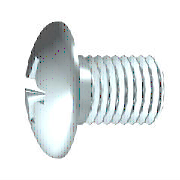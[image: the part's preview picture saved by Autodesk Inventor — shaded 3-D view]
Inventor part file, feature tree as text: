
AUTODESK INVENTOR PART (.ipt)
format: ipt  version: 2015 (Build 190159000, 159)  size: 271,360 bytes
history: native  units: mm (DEFAULTED — no unit token found)
features: sketch x1, plane x1, extrude x1, other x1
ambient origin geometry x7: Origin, YZ Plane, XZ Plane, X Axis, Y Axis, Z Axis, Center Point
bodies: Solid1 (feature_tree), Body (feature_tree)
feature tree (4):
  sketch  "Sketch1"  dims[d1=3.0mm d2=1.96mm d15=90.0deg d3=-2.4mm d4=45.0deg d5=0.966667mm d6=2.9mm d7=0.37mm d8=15.0mm d9=0.0mm d12=10.821041mm d13=4.625123mm d16=2.9mm d17=1.45mm d52=10.0mm d18=0.872665mm d54=90.0deg d19=0.148mm d20=0.0mm d21=3.0mm d22=15.0mm d23=0.306725mm d24=2.4mm d25=5.0mm d27=1.0mm d29=5.6mm d30=16.0mm d72=0.0mm d73=0.0mm d74=0.1mm]
  plane  "Workplane"
  extrude  "Slot"  Depth=0.1mm
  other  "Cut"
